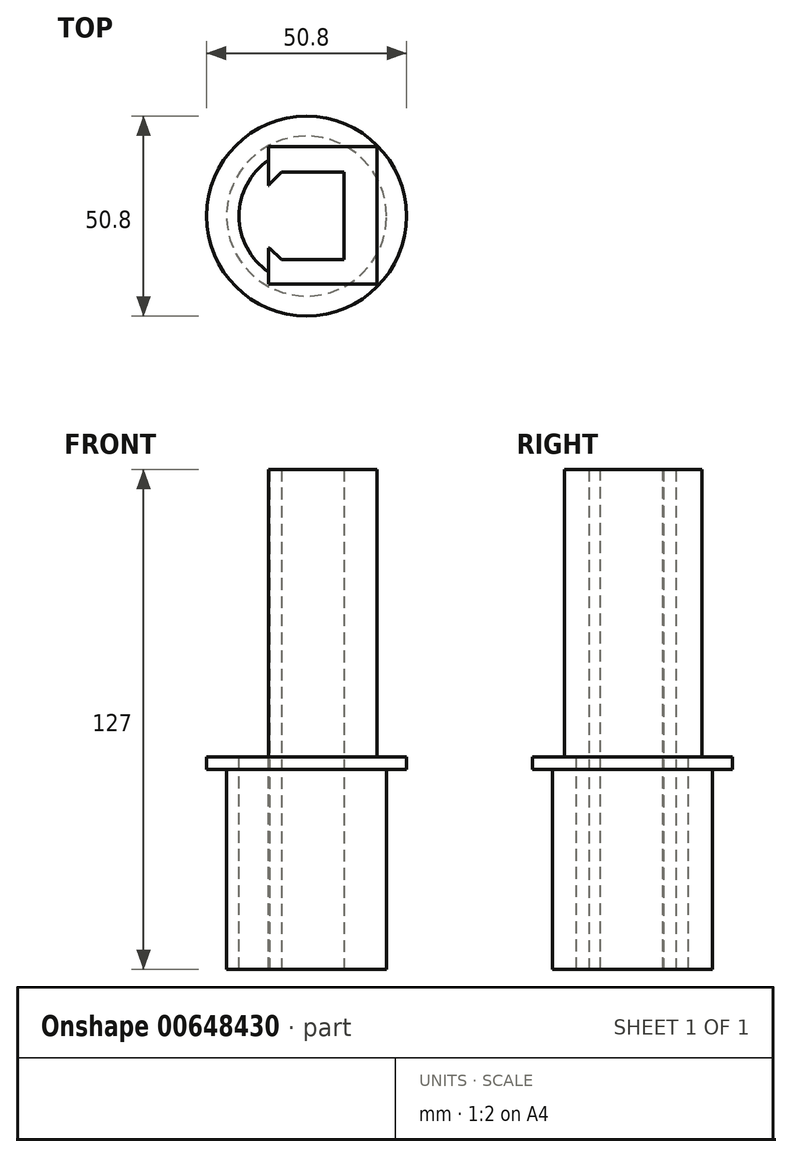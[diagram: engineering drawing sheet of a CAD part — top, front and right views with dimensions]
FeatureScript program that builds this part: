
annotation { "Feature Type Name" : "Feature", "Feature Type Description" : "" }
export const myFeature = defineFeature(function(context is Context, id is Id, definition is map)
    precondition{}
    {
        {
            var Q0;
            Q0=qCreatedBy(makeId("Top.planeOp"),FACE);
            var sketch = newSketch(context, id + "F0", { "sketchPlane" : qUnion([Q0])});
            skCircle(sketch, "E0", {"center": v(0, 0) * mm, "radius": 20.32 * mm});
            skCircle(sketch, "E1", {"center": v(0, 0) * mm, "radius": 17.15 * mm});
            skSolve(sketch);
        }
        {
            var Q0;
            Q0=qCreatedBy(makeId("Top.planeOp"),FACE);
            var sketch = newSketch(context, id + "F1", { "sketchPlane" : qUnion([Q0])});
            skCircle(sketch, "E2", {"center": v(0, 0) * mm, "radius": 25.4 * mm});
            skCircle(sketch, "E3", {"center": v(0, 0) * mm, "radius": 17.15 * mm});
            skSolve(sketch);
        }
        {
            var Q0;
            Q0 = qSketchRegion(id + "F0", true);
            extrude(context, id + "F2", {"entities" : qUnion([Q0]), "oppositeDirection" : true, "depth" : 50.8 * mm, "offsetDistance" : 25.4 * mm});
        }
        {
            var Q0;
            Q0 = qSketchRegion(id + "F1", true);
            extrude(context, id + "F3", {"entities" : qUnion([Q0]), "operationType" : NewBodyOperationType.ADD, "depth" : 3.17 * mm, "offsetDistance" : 25.4 * mm});
        }
        {
            var Q0;
            Q0=qCreatedBy(makeId("Top.planeOp"),FACE);
            var sketch = newSketch(context, id + "F4", { "sketchPlane" : qUnion([Q0])});
            skLineSegment(sketch, "E4.bottom", {"start": v(9.53, -11.11) * mm, "end": v(-9.52, -11.11) * mm});
            skLineSegment(sketch, "E4.top", {"start": v(9.52, 11.11) * mm, "end": v(-9.52, 11.11) * mm});
            skLineSegment(sketch, "E4.left", {"start": v(9.53, -11.11) * mm, "end": v(9.52, 11.11) * mm});
            skLineSegment(sketch, "E4.right", {"start": v(-9.52, -11.11) * mm, "end": v(-9.53, 11.11) * mm});
            skPoint(sketch, "E4.middle", {"position": v(0, 0) * mm});
            skLineSegment(sketch, "E5", {"start": v(-9.52, 7.94) * mm, "end": v(-6.35, 11.11) * mm});
            skLineSegment(sketch, "E6", {"start": v(-9.53, -7.94) * mm, "end": v(-6.35, -11.11) * mm});
            skLineSegment(sketch, "E7.bottom", {"start": v(-9.63, -17.32) * mm, "end": v(17.95, -17.32) * mm});
            skLineSegment(sketch, "E7.top", {"start": v(-9.63, 17.63) * mm, "end": v(17.95, 17.63) * mm});
            skLineSegment(sketch, "E7.left", {"start": v(-9.63, -17.32) * mm, "end": v(-9.63, 17.63) * mm});
            skLineSegment(sketch, "E7.right", {"start": v(17.95, -17.32) * mm, "end": v(17.95, 17.63) * mm});
            skSolve(sketch);
        }
        {
            var Q0;
            Q0 = qSketchRegion(id + "F4", true);
            var Q1;
            {var subQ3=sQuery(id+"F4.wireOp",EDGE,"E6");Q1=makeQuery(id+"F4.imprint","IMPRINT",FACE,{"disambiguationData":[TD([[makeQuery(id+"F4.imprint","IMPRINT",EDGE,{"derivedFrom":subQ3}),-1.0]])]});}
            var Q2;
            {var subQ3=sQuery(id+"F4.wireOp",EDGE,"E5");Q2=makeQuery(id+"F4.imprint","IMPRINT",FACE,{"disambiguationData":[TD([[makeQuery(id+"F4.imprint","IMPRINT",EDGE,{"derivedFrom":subQ3}),1.0]])]});}
            extrude(context, id + "F5", {"entities" : qUnion([Q0, Q1, Q2]), "operationType" : NewBodyOperationType.ADD, "depth" : 76.2 * mm, "offsetDistance" : 25.4 * mm, "hasSecondDirection" : true, "secondDirectionOppositeDirection" : true, "secondDirectionDepth" : 50.8 * mm});
        }
        {
            var Q0;
            Q0=qCreatedBy(makeId("Top.planeOp"),FACE);
            var sketch = newSketch(context, id + "F6", { "sketchPlane" : qUnion([Q0])});
            skCircle(sketch, "E8", {"center": v(0, 0) * mm, "radius": 20.32 * mm});
            skCircle(sketch, "E9", {"center": v(0, 0) * mm, "radius": 34.08 * mm});
            skSolve(sketch);
        }
        {
            var Q0;
            Q0 = qSketchRegion(id + "F6", true);
            extrude(context, id + "F7", {"entities" : qUnion([Q0]), "operationType" : NewBodyOperationType.REMOVE, "oppositeDirection" : true, "depth" : 76.2 * mm, "offsetDistance" : 25.4 * mm});
        }
        {
            var Q0;
            Q0=qCreatedBy(makeId("Top.planeOp"),FACE);
            var sketch = newSketch(context, id + "F8", { "sketchPlane" : qUnion([Q0])});
            skLineSegment(sketch, "E10.bottom", {"start": v(-12.16, 7.8) * mm, "end": v(-3.15, 7.8) * mm});
            skLineSegment(sketch, "E10.top", {"start": v(-12.16, -8.08) * mm, "end": v(-3.15, -8.08) * mm});
            skLineSegment(sketch, "E10.left", {"start": v(-12.16, 7.8) * mm, "end": v(-12.16, -8.08) * mm});
            skLineSegment(sketch, "E10.right", {"start": v(-3.15, 7.8) * mm, "end": v(-3.15, -8.08) * mm});
            skSolve(sketch);
        }
        {
            var Q0;
            Q0 = qSketchRegion(id + "F8", true);
            extrude(context, id + "F9", {"entities" : qUnion([Q0]), "operationType" : NewBodyOperationType.REMOVE, "oppositeDirection" : true, "depth" : 76.2 * mm, "offsetDistance" : 25.4 * mm, "hasSecondDirection" : true, "secondDirectionOppositeDirection" : false, "secondDirectionDepth" : 76.2 * mm});
        }
    });
